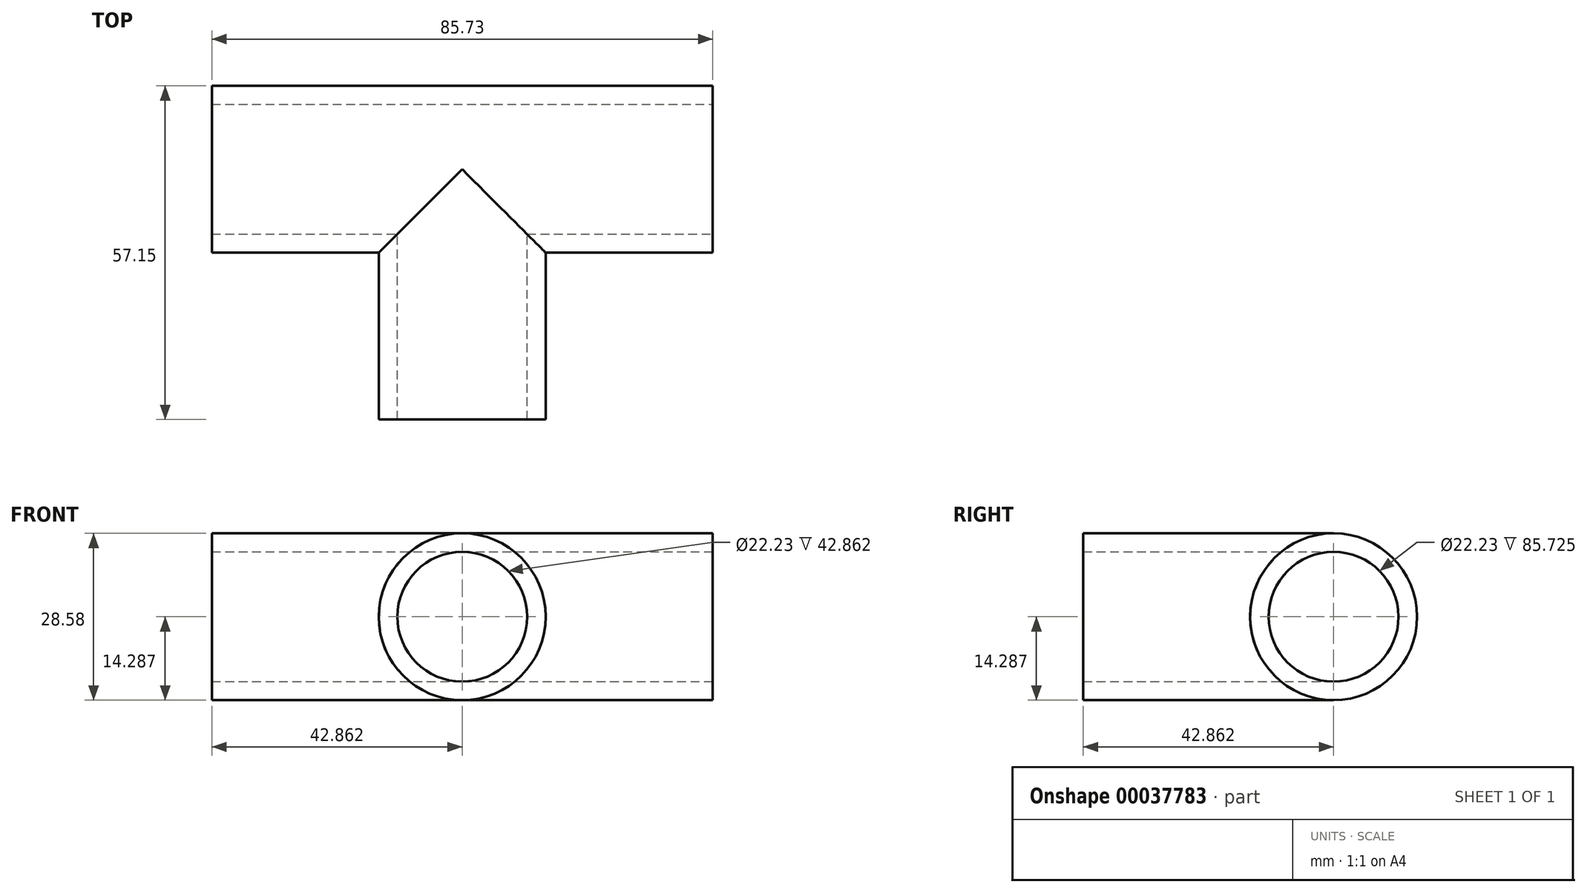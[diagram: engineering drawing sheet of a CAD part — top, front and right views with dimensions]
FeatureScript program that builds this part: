
annotation { "Feature Type Name" : "Feature", "Feature Type Description" : "" }
export const myFeature = defineFeature(function(context is Context, id is Id, definition is map)
    precondition{}
    {
        {
            var Q0;
            Q0=qCreatedBy(makeId("Top.planeOp"),FACE);
            var sketch = newSketch(context, id + "F0", { "sketchPlane" : qUnion([Q0])});
            skLineSegment(sketch, "E0.bottom", {"start": v(0, 0) * mm, "end": v(85.73, 0) * mm});
            skLineSegment(sketch, "E0.left", {"start": v(28.58, -28.58) * mm, "end": v(28.58, -57.15) * mm});
            skLineSegment(sketch, "E1.top", {"start": v(85.73, -28.58) * mm, "end": v(57.15, -28.58) * mm});
            skLineSegment(sketch, "E1.right", {"start": v(57.15, -57.15) * mm, "end": v(57.15, -28.58) * mm});
            skLineSegment(sketch, "E2", {"start": v(28.58, -57.15) * mm, "end": v(57.15, -57.15) * mm});
            skLineSegment(sketch, "E3", {"start": v(85.73, -28.58) * mm, "end": v(85.73, 0) * mm});
            skLineSegment(sketch, "E4", {"start": v(0, 0) * mm, "end": v(0, -28.58) * mm});
            skLineSegment(sketch, "E5", {"start": v(0, -28.58) * mm, "end": v(28.58, -28.58) * mm});
            skSolve(sketch);
        }
        {
            var Q0;
            Q0=qSketchRegion(id+"F0",true);
            extrude(context, id + "F1", {"entities" : qUnion([Q0]), "depth" : 28.57 * mm});
        }
        {
            var Q0;
            Q0=makeQuery(id+"F1.opExtrude","CAP_EDGE",EDGE,{"disambiguationData":[OSD([sQuery(id+"F0.wireOp",EDGE,"E1.right")])],"isStart":false});
            var Q1;
            Q1=makeQuery(id+"F1.opExtrude","CAP_EDGE",EDGE,{"disambiguationData":[OSD([sQuery(id+"F0.wireOp",EDGE,"E1.top")])],"isStart":false});
            var Q2;
            Q2=makeQuery(id+"F1.opExtrude","CAP_EDGE",EDGE,{"disambiguationData":[OSD([sQuery(id+"F0.wireOp",EDGE,"E1.top")])],"isStart":true});
            var Q3;
            Q3=makeQuery(id+"F1.opExtrude","CAP_EDGE",EDGE,{"disambiguationData":[OSD([sQuery(id+"F0.wireOp",EDGE,"E1.right")])],"isStart":true});
            var Q4;
            Q4=makeQuery(id+"F1.opExtrude","CAP_EDGE",EDGE,{"disambiguationData":[OSD([sQuery(id+"F0.wireOp",EDGE,"E0.bottom")])],"isStart":false});
            var Q5;
            Q5=makeQuery(id+"F1.opExtrude","CAP_EDGE",EDGE,{"disambiguationData":[OSD([sQuery(id+"F0.wireOp",EDGE,"E0.left")])],"isStart":true});
            var Q6;
            Q6=makeQuery(id+"F1.opExtrude","CAP_EDGE",EDGE,{"disambiguationData":[OSD([sQuery(id+"F0.wireOp",EDGE,"E0.left")])],"isStart":false});
            var Q7;
            Q7=makeQuery(id+"F1.opExtrude","CAP_EDGE",EDGE,{"disambiguationData":[OSD([sQuery(id+"F0.wireOp",EDGE,"E0.bottom")])],"isStart":true});
            var Q8;
            Q8=makeQuery(id+"F1.opExtrude","CAP_EDGE",EDGE,{"disambiguationData":[OSD([sQuery(id+"F0.wireOp",EDGE,"E5")])],"isStart":true});
            var Q9;
            Q9=makeQuery(id+"F1.opExtrude","CAP_EDGE",EDGE,{"disambiguationData":[OSD([sQuery(id+"F0.wireOp",EDGE,"E5")])],"isStart":false});
            fillet(context, id + "F2", {"entities" : qUnion([Q0, Q1, Q2, Q3, Q4, Q5, Q6, Q7, Q8, Q9]), "radius" : 14.29 * mm, "tangentPropagation" : true, "allowEdgeOverflow" : false});
        }
        {
            var Q0;
            Q0=makeQuery(id+"F1.opExtrude","SWEPT_FACE",FACE,{"disambiguationData":[OSD([sQuery(id+"F0.wireOp",EDGE,"E3")])]});
            shell(context, id + "F3", {"entities" : qUnion([Q0]), "thickness" : 3.17 * mm});
        }
        {
            var Q0;
            Q0=makeQuery(id+"F1.opExtrude","SWEPT_FACE",FACE,{"disambiguationData":[OSD([sQuery(id+"F0.wireOp",EDGE,"E4")])]});
            var sketch = newSketch(context, id + "F4", { "sketchPlane" : qUnion([Q0])});
            skCircle(sketch, "E6", {"center": v(14.29, 14.29) * mm, "radius": 11.11 * mm});
            skSolve(sketch);
        }
        {
            var Q0;
            Q0=qSketchRegion(id+"F4",true);
            extrude(context, id + "F5", {"entities" : qUnion([Q0]), "operationType" : NewBodyOperationType.REMOVE, "oppositeDirection" : true, "depth" : 3.17 * mm});
        }
        {
            var Q0;
            Q0=makeQuery(id+"F1.opExtrude","SWEPT_FACE",FACE,{"disambiguationData":[OSD([sQuery(id+"F0.wireOp",EDGE,"E2")])]});
            var sketch = newSketch(context, id + "F6", { "sketchPlane" : qUnion([Q0])});
            skCircle(sketch, "E7", {"center": v(42.86, 14.29) * mm, "radius": 11.11 * mm});
            skSolve(sketch);
        }
        {
            var Q0;
            Q0 = qSketchRegion(id + "F6", true);
            extrude(context, id + "F7", {"entities" : qUnion([Q0]), "operationType" : NewBodyOperationType.REMOVE, "oppositeDirection" : true, "depth" : 3.17 * mm});
        }
    });
